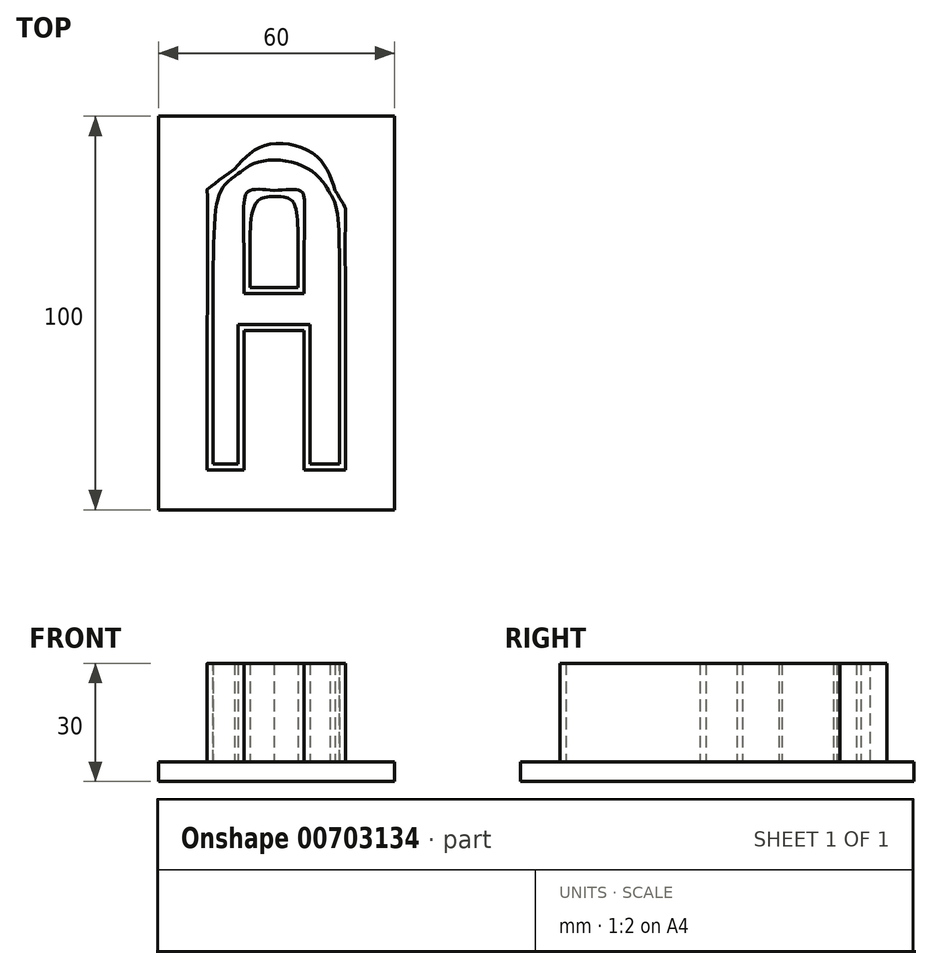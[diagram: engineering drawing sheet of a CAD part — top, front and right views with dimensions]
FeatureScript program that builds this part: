
annotation { "Feature Type Name" : "Feature", "Feature Type Description" : "" }
export const myFeature = defineFeature(function(context is Context, id is Id, definition is map)
    precondition{}
    {
        {
            var Q0;
            Q0=qCreatedBy(makeId("Top.planeOp"),FACE);
            var sketch = newSketch(context, id + "F0", { "sketchPlane" : qUnion([Q0])});
            skLineSegment(sketch, "E0.bottom", {"start": v(30, 50) * mm, "end": v(-30, 50) * mm});
            skLineSegment(sketch, "E0.top", {"start": v(30, -50) * mm, "end": v(-30, -50) * mm});
            skLineSegment(sketch, "E0.left", {"start": v(30, 50) * mm, "end": v(30, -50) * mm});
            skLineSegment(sketch, "E0.right", {"start": v(-30, 50) * mm, "end": v(-30, -50) * mm});
            skPoint(sketch, "E0.middle", {"position": v(0, 0) * mm});
            skSolve(sketch);
        }
        {
            var Q0;
            Q0=makeQuery(id+"F0.imprint","IMPRINT",FACE,{"disambiguationData":[TD([[makeQuery(id+"F0.imprint","IMPRINT",EDGE,{"derivedFrom":sQuery(id+"F0.wireOp",EDGE,"E0.bottom")}),1.0]])]});
            extrude(context, id + "F1", {"entities" : qUnion([Q0]), "depth" : 5 * mm, "offsetDistance" : 25 * mm});
        }
        {
            var Q0;
            Q0=makeQuery(id+"F1.opExtrude","CAP_FACE",FACE,{"disambiguationData":[OSD([sQuery(id+"F0.wireOp",EDGE,"E0.bottom"),sQuery(id+"F0.wireOp",EDGE,"E0.top"),sQuery(id+"F0.wireOp",EDGE,"E0.left"),sQuery(id+"F0.wireOp",EDGE,"E0.right")])],"isStart":false});
            var sketch = newSketch(context, id + "F2", { "sketchPlane" : qUnion([Q0])});
            skLineSegment(sketch, "E1", {"start": v(-8.2, -22.18) * mm, "end": v(-8.2, -4.43) * mm});
            skLineSegment(sketch, "E2", {"start": v(-8.2, -4.43) * mm, "end": v(-0.59, -4.43) * mm});
            skLineSegment(sketch, "E3", {"start": v(-0.59, -4.43) * mm, "end": v(7.03, -4.43) * mm});
            skLineSegment(sketch, "E4", {"start": v(7.03, -4.43) * mm, "end": v(7.03, -22.18) * mm});
            skLineSegment(sketch, "E5", {"start": v(7.03, -22.18) * mm, "end": v(7.03, -39.93) * mm});
            skLineSegment(sketch, "E6", {"start": v(7.03, -39.93) * mm, "end": v(12.3, -39.93) * mm});
            skLineSegment(sketch, "E7", {"start": v(12.3, -39.93) * mm, "end": v(17.58, -39.93) * mm});
            skLineSegment(sketch, "E8", {"start": v(17.58, -39.93) * mm, "end": v(17.58, -6.74) * mm});
            skFitSpline(sketch, "E9", {"points": [v(17.58, -6.74) * mm, v(17.58, 25.6) * mm, v(17.5, 26.57) * mm, v(14.94, 31.1) * mm]});
            skFitSpline(sketch, "E10", {"points": [v(14.94, 31.1) * mm, v(9.84, 40.13) * mm, v(-2.43, 42.74) * mm, v(-10.67, 36.56) * mm]});
            skFitSpline(sketch, "E11", {"points": [v(-10.67, 36.56) * mm, v(-17.53, 31.41) * mm, v(-17.58, 31.15) * mm, v(-17.58, -5.94) * mm]});
            skLineSegment(sketch, "E12", {"start": v(-17.58, -5.94) * mm, "end": v(-17.58, -39.93) * mm});
            skLineSegment(sketch, "E13", {"start": v(-17.58, -39.93) * mm, "end": v(-12.89, -39.93) * mm});
            skLineSegment(sketch, "E14", {"start": v(-12.89, -39.93) * mm, "end": v(-8.2, -39.93) * mm});
            skLineSegment(sketch, "E15", {"start": v(-8.2, -39.93) * mm, "end": v(-8.2, -22.18) * mm});
            skFitSpline(sketch, "E16", {"points": [v(-8.2, 15.7) * mm, v(-8.2, 28.37) * mm, v(-6.87, 31.07) * mm, v(-0.6, 31.07) * mm]});
            skFitSpline(sketch, "E17", {"points": [v(-0.6, 31.07) * mm, v(6.1, 31.07) * mm, v(7.03, 29.27) * mm, v(7.03, 16.38) * mm]});
            skLineSegment(sketch, "E18", {"start": v(7.03, 16.38) * mm, "end": v(7.03, 4.97) * mm});
            skLineSegment(sketch, "E19", {"start": v(7.03, 4.97) * mm, "end": v(-0.59, 4.97) * mm});
            skLineSegment(sketch, "E20", {"start": v(-0.59, 4.97) * mm, "end": v(-8.2, 4.97) * mm});
            skLineSegment(sketch, "E21", {"start": v(-8.2, 4.97) * mm, "end": v(-8.2, 15.7) * mm});
            skFitSpline(sketch, "E22.0", {"points": [v(16.08, -6.74) * mm, v(16.08, -2.7) * mm, v(16.07, 4.4) * mm, v(16.04, 12.52) * mm, v(15.93, 18.5) * mm, v(15.74, 22.73) * mm, v(15.44, 25.6) * mm, v(15.02, 27.48) * mm, v(14.47, 28.85) * mm, v(13.95, 29.81) * mm, v(13.63, 30.37) * mm]});
            skLineSegment(sketch, "E22.1", {"start": v(16.08, -38.43) * mm, "end": v(16.08, -6.74) * mm});
            skLineSegment(sketch, "E22.2", {"start": v(12.3, -38.43) * mm, "end": v(16.08, -38.43) * mm});
            skLineSegment(sketch, "E22.3", {"start": v(8.53, -38.43) * mm, "end": v(12.3, -38.43) * mm});
            skLineSegment(sketch, "E22.4", {"start": v(-12.89, -38.43) * mm, "end": v(-9.7, -38.43) * mm});
            skLineSegment(sketch, "E22.5", {"start": v(-16.08, -38.43) * mm, "end": v(-12.89, -38.43) * mm});
            skLineSegment(sketch, "E22.6", {"start": v(-16.08, -5.94) * mm, "end": v(-16.08, -38.43) * mm});
            skFitSpline(sketch, "E22.7", {"points": [v(-9.77, 35.36) * mm, v(-10.63, 34.71) * mm, v(-11.71, 33.9) * mm, v(-12.8, 32.87) * mm, v(-13.45, 32.1) * mm, v(-14, 31.22) * mm, v(-14.47, 30.16) * mm, v(-14.88, 28.81) * mm, v(-15.34, 26.55) * mm, v(-15.74, 22.7) * mm, v(-15.99, 16) * mm, v(-16.07, 6.81) * mm, v(-16.08, -1.3) * mm, v(-16.08, -5.94) * mm]});
            skLineSegment(sketch, "E22.8", {"start": v(-9.7, -38.43) * mm, "end": v(-9.7, -22.18) * mm});
            skLineSegment(sketch, "E22.9", {"start": v(-9.7, -22.18) * mm, "end": v(-9.7, -2.93) * mm});
            skLineSegment(sketch, "E22.10", {"start": v(-9.7, -2.93) * mm, "end": v(-0.59, -2.93) * mm});
            skLineSegment(sketch, "E22.11", {"start": v(-0.59, -2.93) * mm, "end": v(8.53, -2.93) * mm});
            skFitSpline(sketch, "E22.12", {"points": [v(13.63, 30.37) * mm, v(12.47, 32.43) * mm, v(9.33, 35.8) * mm, v(3.09, 38.5) * mm, v(-3.7, 38.57) * mm, v(-7.9, 36.76) * mm, v(-9.77, 35.36) * mm]});
            skLineSegment(sketch, "E22.13", {"start": v(8.53, -2.93) * mm, "end": v(8.53, -22.18) * mm});
            skLineSegment(sketch, "E22.14", {"start": v(8.53, -22.18) * mm, "end": v(8.53, -38.43) * mm});
            skLineSegment(sketch, "E23.0", {"start": v(-6.7, 6.47) * mm, "end": v(-6.7, 15.7) * mm});
            skFitSpline(sketch, "E23.1", {"points": [v(-0.6, 29.57) * mm, v(0.2, 29.57) * mm, v(1.25, 29.53) * mm, v(2.3, 29.36) * mm, v(2.93, 29.18) * mm, v(3.41, 28.96) * mm, v(3.78, 28.7) * mm, v(4.1, 28.37) * mm, v(4.4, 27.9) * mm, v(4.68, 27.25) * mm, v(5.01, 26.1) * mm, v(5.32, 24.12) * mm, v(5.5, 20.83) * mm, v(5.53, 17.98) * mm, v(5.53, 16.38) * mm]});
            skLineSegment(sketch, "E23.2", {"start": v(5.53, 16.38) * mm, "end": v(5.53, 6.47) * mm});
            skFitSpline(sketch, "E23.3", {"points": [v(-6.7, 15.7) * mm, v(-6.7, 17.27) * mm, v(-6.66, 20.09) * mm, v(-6.44, 23.42) * mm, v(-6.02, 25.91) * mm, v(-5.53, 27.3) * mm, v(-5.07, 28.07) * mm, v(-4.71, 28.5) * mm, v(-4.31, 28.82) * mm, v(-3.84, 29.09) * mm, v(-3.25, 29.3) * mm, v(-2.28, 29.5) * mm, v(-1.33, 29.57) * mm, v(-0.6, 29.57) * mm]});
            skLineSegment(sketch, "E23.4", {"start": v(5.53, 6.47) * mm, "end": v(-0.59, 6.47) * mm});
            skLineSegment(sketch, "E23.5", {"start": v(-0.59, 6.47) * mm, "end": v(-6.7, 6.47) * mm});
            skSolve(sketch);
        }
        {
            var Q0;
            Q0=makeQuery(id+"F2.imprint","IMPRINT",FACE,{"disambiguationData":[TD([[makeQuery(id+"F2.imprint","IMPRINT",EDGE,{"derivedFrom":sQuery(id+"F2.wireOp",EDGE,"E1")}),1.0]])]});
            var Q1;
            Q1=makeQuery(id+"F2.imprint","IMPRINT",FACE,{"disambiguationData":[TD([[makeQuery(id+"F2.imprint","IMPRINT",EDGE,{"derivedFrom":sQuery(id+"F2.wireOp",EDGE,"E16")}),-1.0]])]});
            extrude(context, id + "F3", {"entities" : qUnion([Q0, Q1]), "operationType" : NewBodyOperationType.ADD, "depth" : 25 * mm, "offsetDistance" : 25 * mm});
        }
    });
